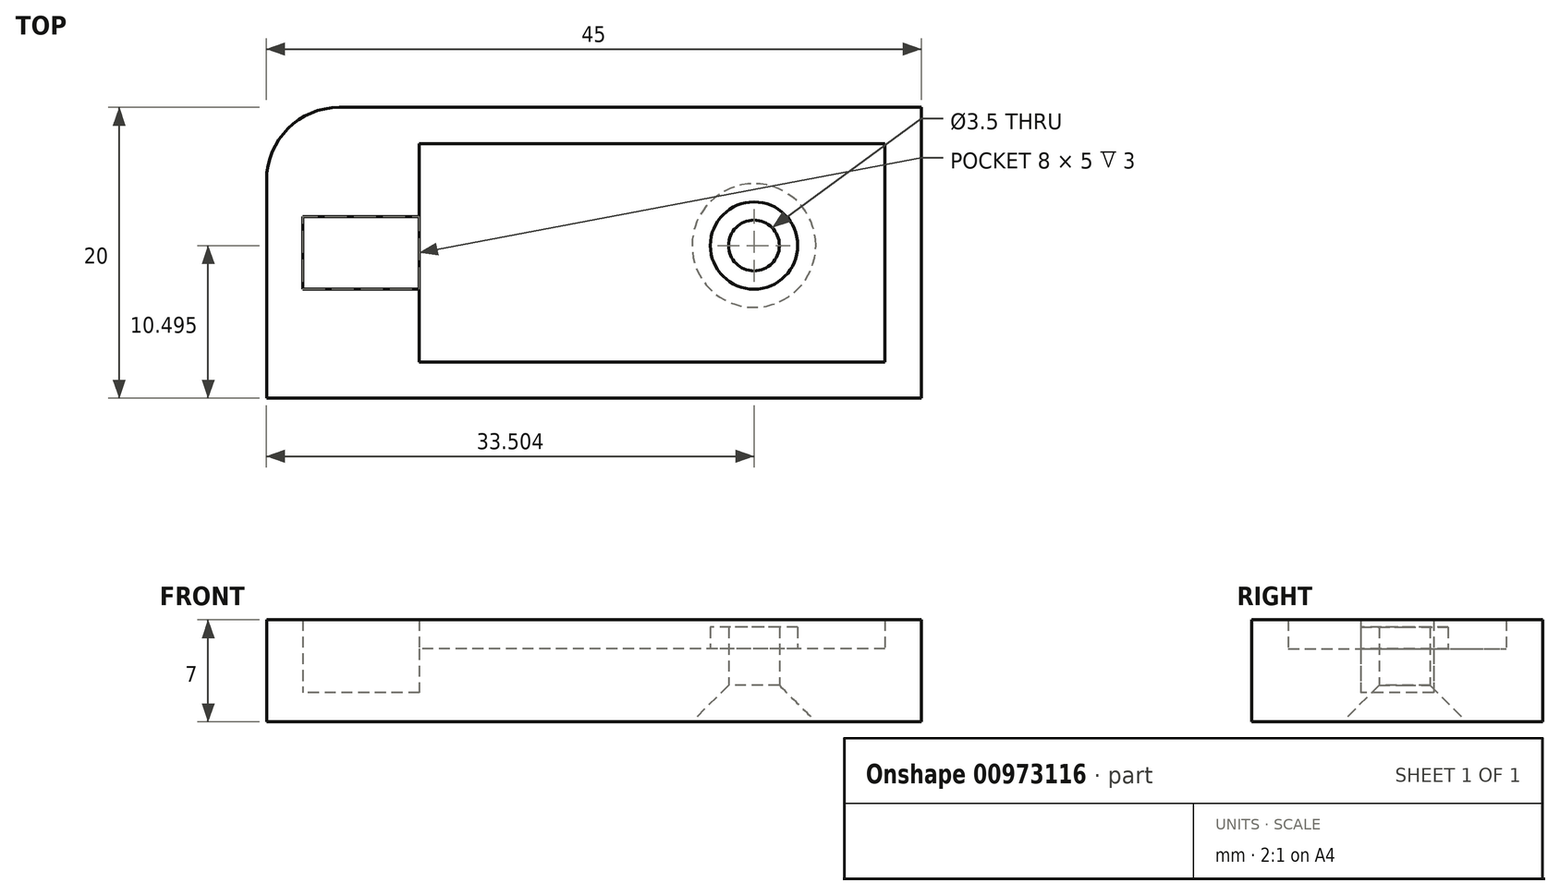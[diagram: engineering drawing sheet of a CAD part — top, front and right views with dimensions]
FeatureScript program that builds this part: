
annotation { "Feature Type Name" : "Feature", "Feature Type Description" : "" }
export const myFeature = defineFeature(function(context is Context, id is Id, definition is map)
    precondition{}
    {
        {
            var Q0;
            Q0=qCreatedBy(makeId("Top.planeOp"),FACE);
            var sketch = newSketch(context, id + "F0", { "sketchPlane" : qUnion([Q0])});
            skLineSegment(sketch, "E0.bottom", {"start": v(-23, 39.55) * mm, "end": v(22, 39.55) * mm});
            skLineSegment(sketch, "E0.top", {"start": v(-23, 19.55) * mm, "end": v(22, 19.55) * mm});
            skLineSegment(sketch, "E0.left", {"start": v(-23, 39.55) * mm, "end": v(-23, 19.55) * mm});
            skLineSegment(sketch, "E0.right", {"start": v(22, 39.55) * mm, "end": v(22, 19.55) * mm});
            skLineSegment(sketch, "E1.bottom", {"start": v(-9.93, 19.55) * mm, "end": v(10.07, 19.55) * mm});
            skLineSegment(sketch, "E1.top", {"start": v(-9.93, -0.45) * mm, "end": v(10.07, -0.45) * mm});
            skLineSegment(sketch, "E1.left", {"start": v(-9.93, 19.55) * mm, "end": v(-9.93, -0.45) * mm});
            skLineSegment(sketch, "E1.right", {"start": v(10.07, 19.55) * mm, "end": v(10.07, -0.45) * mm});
            skLineSegment(sketch, "E2", {"start": v(-9.93, 4.55) * mm, "end": v(10.07, 4.55) * mm});
            skLineSegment(sketch, "E3.bottom", {"start": v(-12.5, 37.05) * mm, "end": v(19.5, 37.05) * mm});
            skLineSegment(sketch, "E3.top", {"start": v(-12.5, 22.05) * mm, "end": v(19.5, 22.05) * mm});
            skLineSegment(sketch, "E3.left", {"start": v(-12.5, 37.05) * mm, "end": v(-12.5, 22.05) * mm});
            skLineSegment(sketch, "E3.right", {"start": v(19.5, 37.05) * mm, "end": v(19.5, 22.05) * mm});
            skLineSegment(sketch, "E4.bottom", {"start": v(-12.5, 32.05) * mm, "end": v(-20.5, 32.05) * mm});
            skLineSegment(sketch, "E4.top", {"start": v(-12.5, 27.05) * mm, "end": v(-20.5, 27.05) * mm});
            skLineSegment(sketch, "E4.left", {"start": v(-12.5, 32.05) * mm, "end": v(-12.5, 27.05) * mm});
            skLineSegment(sketch, "E4.right", {"start": v(-20.5, 32.05) * mm, "end": v(-20.5, 27.05) * mm});
            skLineSegment(sketch, "E5", {"start": v(-16.5, 32.05) * mm, "end": v(-16.5, 27.05) * mm});
            skCircle(sketch, "E6", {"center": v(10.5, 30.05) * mm, "radius": 3 * mm});
            skCircle(sketch, "E7", {"center": v(10.5, 30.05) * mm, "radius": 1.75 * mm});
            skSolve(sketch);
        }
        {
            var Q0;
            Q0=makeQuery(id+"F0.imprint","IMPRINT",FACE,{"disambiguationData":[TD([[makeQuery(id+"F0.imprint","IMPRINT",EDGE,{"derivedFrom":sQuery(id+"F0.wireOp",EDGE,"E0.bottom")}),-1.0]])]});
            var Q1;
            {var subQ0=sQuery(id+"F0.wireOp",EDGE,"E4.right");Q1=makeQuery(id+"F0.imprint","IMPRINT",FACE,{"disambiguationData":[TD([[makeQuery(id+"F0.imprint","IMPRINT",EDGE,{"derivedFrom":subQ0}),1.0]])]});}
            var Q2;
            {var subQ5=sQuery(id+"F0.wireOp",EDGE,"E5");Q2=makeQuery(id+"F0.imprint","IMPRINT",FACE,{"disambiguationData":[TD([[makeQuery(id+"F0.imprint","IMPRINT",EDGE,{"derivedFrom":subQ5}),1.0]])]});}
            var Q3;
            {var subQ3=sQuery(id+"F0.wireOp",EDGE,"E3.bottom");Q3=makeQuery(id+"F0.imprint","IMPRINT",FACE,{"disambiguationData":[TD([[makeQuery(id+"F0.imprint","IMPRINT",EDGE,{"derivedFrom":subQ3}),-1.0]])]});}
            var Q4;
            Q4=makeQuery(id+"F0.imprint","IMPRINT",FACE,{"disambiguationData":[TD([[makeQuery(id+"F0.imprint","IMPRINT",EDGE,{"derivedFrom":sQuery(id+"F0.wireOp",EDGE,"E6")}),1.0]])]});
            extrude(context, id + "F1", {"entities" : qUnion([Q0, Q1, Q2, Q3, Q4]), "depth" : 5 * mm, "offsetDistance" : 25 * mm});
        }
        {
            var Q0;
            Q0=makeQuery(id+"F0.imprint","IMPRINT",FACE,{"disambiguationData":[TD([[makeQuery(id+"F0.imprint","IMPRINT",EDGE,{"derivedFrom":sQuery(id+"F0.wireOp",EDGE,"E0.bottom")}),-1.0]])]});
            extrude(context, id + "F2", {"entities" : qUnion([Q0]), "operationType" : NewBodyOperationType.ADD, "depth" : 7 * mm, "offsetDistance" : 25 * mm});
        }
        {
            var Q0;
            {var subQ0=sQuery(id+"F0.wireOp",EDGE,"E4.right");Q0=makeQuery(id+"F0.imprint","IMPRINT",FACE,{"disambiguationData":[TD([[makeQuery(id+"F0.imprint","IMPRINT",EDGE,{"derivedFrom":subQ0}),1.0]])]});}
            var Q1;
            Q1=makeQuery(id+"F1.opExtrude","CAP_FACE",FACE,{"disambiguationData":[OSD([sQuery(id+"F0.wireOp",EDGE,"E0.bottom"),sQuery(id+"F0.wireOp",EDGE,"E0.top"),sQuery(id+"F0.wireOp",EDGE,"E0.left"),sQuery(id+"F0.wireOp",EDGE,"E0.right"),sQuery(id+"F0.wireOp",EDGE,"E7")])],"isStart":false});
            var Q2;
            {var subQ5=sQuery(id+"F0.wireOp",EDGE,"E5");Q2=makeQuery(id+"F0.imprint","IMPRINT",FACE,{"disambiguationData":[TD([[makeQuery(id+"F0.imprint","IMPRINT",EDGE,{"derivedFrom":subQ5}),1.0]])]});}
            extrude(context, id + "F3", {"entities" : qUnion([Q0, Q1, Q2]), "operationType" : NewBodyOperationType.REMOVE, "depth" : 8.5 * mm, "offsetDistance" : 25 * mm, "hasSecondDirection" : true, "secondDirectionOppositeDirection" : false, "secondDirectionDepth" : 2 * mm});
        }
        {
            var Q0;
            Q0=makeQuery(id+"F1.opExtrude","CAP_EDGE",EDGE,{"disambiguationData":[OSD([sQuery(id+"F0.wireOp",EDGE,"E7")])],"isStart":true});
            chamfer(context, id + "F4", {"entities" : qUnion([Q0]), "width" : 2.5 * mm, "tangentPropagation" : true});
        }
        {
            var Q0;
            Q0=makeQuery(id+"F0.imprint","IMPRINT",FACE,{"disambiguationData":[TD([[makeQuery(id+"F0.imprint","IMPRINT",EDGE,{"derivedFrom":sQuery(id+"F0.wireOp",EDGE,"E6")}),1.0]])]});
            extrude(context, id + "F5", {"entities" : qUnion([Q0]), "operationType" : NewBodyOperationType.ADD, "depth" : 6.5 * mm, "offsetDistance" : 25 * mm, "hasSecondDirection" : true, "secondDirectionOppositeDirection" : false, "secondDirectionDepth" : 5 * mm});
        }
        {
            var Q0;
            {var subQ0=sQuery(id+"F0.wireOp",EDGE,"E0.left");var subQ1=sQuery(id+"F0.wireOp",EDGE,"E0.bottom");Q0=makeQuery(id+"F2.boolean.opBoolean","MERGE",EDGE,{"derivedFrom":[makeQuery(id+"F1.opExtrude","SWEPT_EDGE",EDGE,{"disambiguationData":[OSD([subQ1,subQ0])]}),makeQuery(id+"F2.opExtrude","SWEPT_EDGE",EDGE,{"disambiguationData":[OSD([subQ1,subQ0])]})]});}
            fillet(context, id + "F6", {"entities" : qUnion([Q0]), "radius" : 5 * mm, "tangentPropagation" : true, "allowEdgeOverflow" : false});
        }
    });
